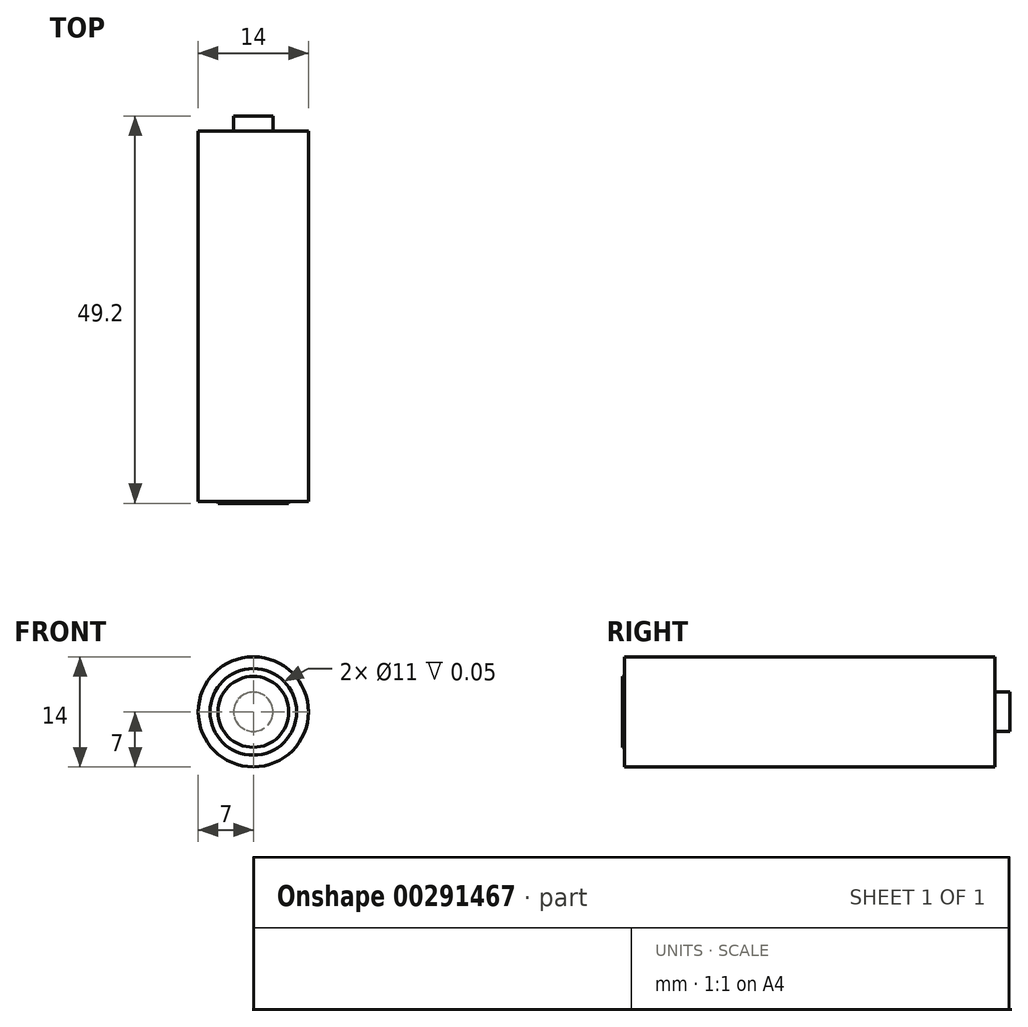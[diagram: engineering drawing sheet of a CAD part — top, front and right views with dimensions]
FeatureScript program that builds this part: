
annotation { "Feature Type Name" : "Feature", "Feature Type Description" : "" }
export const myFeature = defineFeature(function(context is Context, id is Id, definition is map)
    precondition{}
    {
        {
            var Q0;
            Q0=qCreatedBy(makeId("Front.planeOp"),FACE);
            var sketch = newSketch(context, id + "F0", { "sketchPlane" : qUnion([Q0])});
            skCircle(sketch, "E0", {"center": v(0, 0) * mm, "radius": 7 * mm});
            skCircle(sketch, "E1", {"center": v(0, 0) * mm, "radius": 5.5 * mm});
            skSolve(sketch);
        }
        {
            var Q0;
            Q0=makeQuery(id+"F0.imprint","IMPRINT",FACE,{"disambiguationData":[TD([[makeQuery(id+"F0.imprint","IMPRINT",EDGE,{"derivedFrom":sQuery(id+"F0.wireOp",EDGE,"E0")}),1.0]])]});
            extrude(context, id + "F1", {"entities" : qUnion([Q0]), "endBound" : BoundingType.SYMMETRIC, "depth" : 47 * mm});
        }
        {
            var Q0;
            Q0=makeQuery(id+"F0.imprint","IMPRINT",FACE,{"disambiguationData":[TD([[makeQuery(id+"F0.imprint","IMPRINT",EDGE,{"derivedFrom":sQuery(id+"F0.wireOp",EDGE,"E1")}),1.0]])]});
            extrude(context, id + "F2", {"entities" : qUnion([Q0]), "operationType" : NewBodyOperationType.ADD, "endBound" : BoundingType.SYMMETRIC, "depth" : 46.9 * mm});
        }
        {
            var Q0;
            Q0=makeQuery(id+"F2.opExtrude","CAP_FACE",FACE,{"disambiguationData":[OSD([sQuery(id+"F0.wireOp",EDGE,"E1")])],"isStart":false});
            var sketch = newSketch(context, id + "F3", { "sketchPlane" : qUnion([Q0])});
            skCircle(sketch, "E2", {"center": v(0, 0) * mm, "radius": 4.5 * mm});
            skSolve(sketch);
        }
        {
            var Q0;
            Q0 = qSketchRegion(id + "F3", true);
            extrude(context, id + "F4", {"entities" : qUnion([Q0]), "operationType" : NewBodyOperationType.ADD, "depth" : 0.3 * mm});
        }
        {
            var Q0;
            Q0=makeQuery(id+"F2.opExtrude","CAP_FACE",FACE,{"disambiguationData":[OSD([sQuery(id+"F0.wireOp",EDGE,"E1")])],"isStart":true});
            var sketch = newSketch(context, id + "F5", { "sketchPlane" : qUnion([Q0])});
            skCircle(sketch, "E3", {"center": v(0, 0) * mm, "radius": 2.5 * mm});
            skSolve(sketch);
        }
        {
            var Q0;
            Q0=makeQuery(id+"F5.imprint","IMPRINT",FACE,{"disambiguationData":[TD([[makeQuery(id+"F5.imprint","IMPRINT",EDGE,{"derivedFrom":sQuery(id+"F5.wireOp",EDGE,"E3")}),1.0]])]});
            extrude(context, id + "F6", {"entities" : qUnion([Q0]), "operationType" : NewBodyOperationType.ADD, "depth" : 2 * mm});
        }
    });
